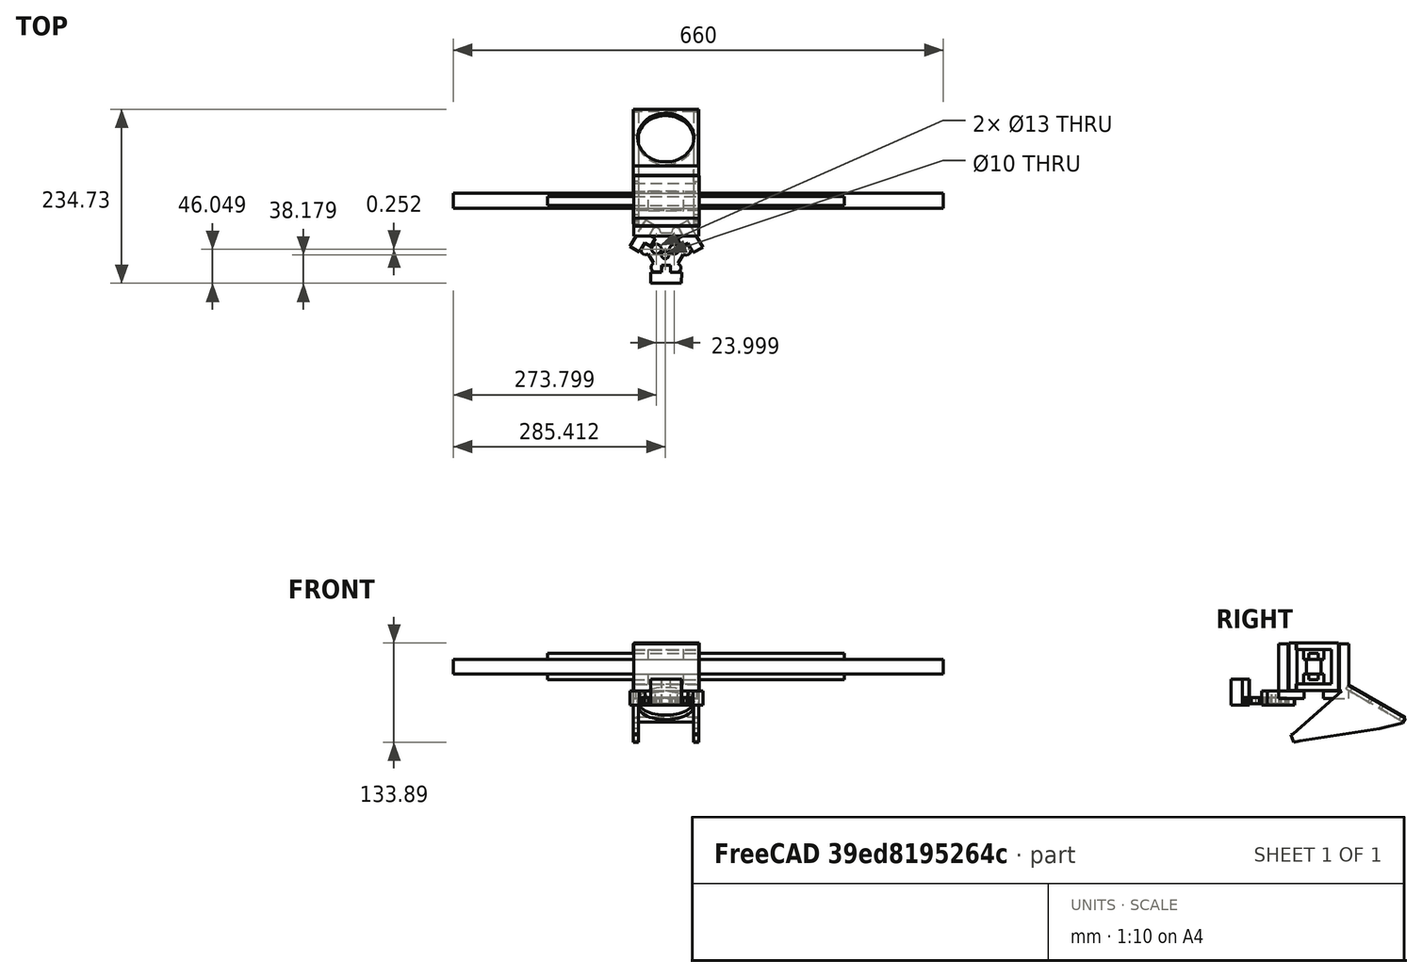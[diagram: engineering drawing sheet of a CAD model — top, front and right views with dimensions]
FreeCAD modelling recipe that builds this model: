
FCSTD DOCUMENT  (FreeCAD 0.17R13522 (Git))
Label: plateX
License: All rights reserved
LicenseURL: http://en.wikipedia.org/wiki/All_rights_reserved
objects: Sketcher::SketchObject×26, Part::Extrusion×26, Part::Box×10, Mesh::Feature×8, Part::MultiFuse×4, App::DocumentObjectGroup×2
note: 66 computed .brp shape members not serialized (recipe doc carries the construction recipe); baked Part::Feature solids carry a one-line shape summary decoded from their .brp

FEATURE [Part::Box] Box  label="vSlot2020"
  AttacherType = Attacher::AttachEngine3D
  Height = 20
  Length = 660
  Placement = pos=(-70,0.5,0) rot=(0,0,1;0rad)
  Width = 20
FEATURE [Part::Box] Box002  label="Rail superior"
  AttacherType = Attacher::AttachEngine3D
  Height = 7.8
  Length = 400
  Placement = pos=(57,4,20) rot=(0,0,1;0rad)
  Width = 12.2
FEATURE [Part::Box] Box004  label="Rail inferior"
  AttacherType = Attacher::AttachEngine3D
  Height = 7.8
  Length = 400
  Placement = pos=(57,4,-7.8) rot=(0,0,1;0rad)
  Width = 12.2
FEATURE [Part::Box] Box005  label="Mgn12h inferior"
  AttacherType = Attacher::AttachEngine3D
  Height = 13
  Length = 47.55
  Placement = pos=(193,-3,-13) rot=(0,0,1;0rad)
  Width = 27.1
FEATURE [Part::Box] Box013  label="Mgn12h superior"
  AttacherType = Attacher::AttachEngine3D
  Height = 13
  Length = 47.55
  Placement = pos=(193,-3,20) rot=(0,0,1;0rad)
  Width = 27.1
FEATURE [Sketcher::SketchObject] Sketch
  sketch-geometry (8):
    g0: LineSegment StartX=64.0547 StartY=96.1652 StartZ=0 EndX=64.0547 EndY=32.1652 EndZ=0
    g1: LineSegment StartX=64.0547 StartY=32.1652 StartZ=0 EndX=121.055 EndY=32.1652 EndZ=0
    g2: LineSegment StartX=121.055 StartY=32.1652 StartZ=0 EndX=121.055 EndY=41.1652 EndZ=0
    g3: LineSegment StartX=121.055 StartY=41.1652 StartZ=0 EndX=74.0547 EndY=41.1652 EndZ=0
    g4: LineSegment StartX=74.0547 StartY=41.1652 StartZ=0 EndX=74.0547 EndY=87.1652 EndZ=0
    g5: LineSegment StartX=74.0547 StartY=87.1652 StartZ=0 EndX=121.055 EndY=87.1652 EndZ=0
    g6: LineSegment StartX=121.055 StartY=87.1652 StartZ=0 EndX=121.055 EndY=96.1652 EndZ=0
    g7: LineSegment StartX=121.055 StartY=96.1652 StartZ=0 EndX=64.0547 EndY=96.1652 EndZ=0
  constraints (22):
    c: Vertical(g0)
    c: Coincident(g0,g1)
    c: Horizontal(g1)
    c: Coincident(g1,g2)
    c: Vertical(g2)
    c: Coincident(g2,g3)
    c: Horizontal(g3)
    c: Coincident(g3,g4)
    c: Vertical(g4)
    c: Coincident(g4,g5)
    c: Horizontal(g5)
    c: Coincident(g5,g6)
    c: Coincident(g6,g7)
    c: Coincident(g7,g0)
    c: Horizontal(g7)
    c: Equal(g7,g1)
    c: Equal(g5,g3)
    c: Equal(g6,g2)
    c: DistanceY(g0,g0) = 64
    c: DistanceX(g7,g7) = 57
    c: DistanceX(g5,g5) = 47
    c: DistanceY(g4,g4) = 46
FEATURE [Part::Extrusion] Extrude  label="PlateX_01"
  Base = -> Sketch
  Dir = (0,0,1)
  DirMode = 2
  FaceMakerClass = Part::FaceMakerBullseye
  LengthFwd = 88
  LengthRev = 0
  Placement = pos=(173,108,74) rot=(0.57735,-0.57735,0.57735;4.18879rad)
  Solid = true
  Symmetric = false
FEATURE [Sketcher::SketchObject] Sketch001
  sketch-geometry (39):
    g0: LineSegment StartX=92.1382 StartY=71.478 StartZ=0 EndX=99.1382 EndY=59.3536 EndZ=0
    g1: LineSegment StartX=68.3387 StartY=30.9498 StartZ=0 EndX=82.3387 EndY=30.9498 EndZ=0
    g2: LineSegment StartX=59.14 StartY=71.8249 StartZ=0 EndX=52.14 EndY=59.7005 EndZ=0
    g3: LineSegment StartX=82.3387 StartY=30.9498 StartZ=0 EndX=83.7847 EndY=26.0283 EndZ=0
    g4: LineSegment StartX=83.7847 StartY=26.0283 StartZ=0 EndX=87.6579 EndY=23.7374 EndZ=0
    g5: LineSegment StartX=87.6579 StartY=23.7374 StartZ=0 EndX=92.6674 EndY=24.8409 EndZ=0
    g6: LineSegment StartX=92.6674 StartY=24.8409 StartZ=0 EndX=98.0127 EndY=33.8785 EndZ=0
    g7: LineSegment StartX=98.0127 StartY=33.8785 StartZ=0 EndX=90.2662 EndY=38.4602 EndZ=0
    g8: LineSegment StartX=90.2662 StartY=38.4602 StartZ=0 EndX=96.3751 EndY=48.7888 EndZ=0
    g9: LineSegment StartX=96.3751 StartY=48.7888 StartZ=0 EndX=104.122 EndY=44.2072 EndZ=0
    g10: LineSegment StartX=104.122 StartY=44.2072 StartZ=0 EndX=109.467 EndY=53.2447 EndZ=0
    g11: LineSegment StartX=109.467 StartY=53.2447 StartZ=0 EndX=108.021 EndY=58.1663 EndZ=0
    g12: LineSegment StartX=108.021 StartY=58.1663 StartZ=0 EndX=104.148 EndY=60.4571 EndZ=0
    g13: LineSegment StartX=104.148 StartY=60.4571 StartZ=0 EndX=99.1382 EndY=59.3536 EndZ=0
    g14: LineSegment StartX=92.1382 StartY=71.478 StartZ=0 EndX=95.6774 EndY=75.191 EndZ=0
    g15: LineSegment StartX=95.6774 StartY=75.191 StartZ=0 EndX=95.7247 EndY=79.6908 EndZ=0
    g16: LineSegment StartX=95.7247 StartY=79.6908 StartZ=0 EndX=92.2644 EndY=83.4773 EndZ=0
    g17: LineSegment StartX=92.2644 StartY=83.4773 StartZ=0 EndX=81.7649 EndY=83.5877 EndZ=0
    g18: LineSegment StartX=81.7649 StartY=83.5877 StartZ=0 EndX=81.6703 EndY=74.5882 EndZ=0
    g19: LineSegment StartX=81.6703 StartY=74.5882 StartZ=0 EndX=69.671 EndY=74.7143 EndZ=0
    g20: LineSegment StartX=69.671 StartY=74.7143 StartZ=0 EndX=69.7656 EndY=83.7138 EndZ=0
    g21: LineSegment StartX=69.7656 StartY=83.7138 StartZ=0 EndX=59.2662 EndY=83.8242 EndZ=0
    g22: LineSegment StartX=59.2662 StartY=83.8242 StartZ=0 EndX=55.727 EndY=80.1112 EndZ=0
    g23: LineSegment StartX=55.727 StartY=80.1112 StartZ=0 EndX=55.6796 EndY=75.6115 EndZ=0
    g24: LineSegment StartX=55.6796 StartY=75.6115 StartZ=0 EndX=59.14 EndY=71.8249 EndZ=0
    g25: LineSegment StartX=52.14 StartY=59.7005 StartZ=0 EndX=47.1537 EndY=60.9041 EndZ=0
    g26: LineSegment StartX=47.1537 StartY=60.9041 StartZ=0 EndX=43.2331 EndY=58.6952 EndZ=0
    g27: LineSegment StartX=43.2331 StartY=58.6952 StartZ=0 EndX=41.6889 EndY=53.8036 EndZ=0
    g28: LineSegment StartX=41.6889 StartY=53.8036 StartZ=0 EndX=46.8412 EndY=44.6589 EndZ=0
    g29: LineSegment StartX=46.8412 StartY=44.6589 StartZ=0 EndX=54.6823 EndY=49.0767 EndZ=0
    g30: LineSegment StartX=54.6823 StartY=49.0767 StartZ=0 EndX=60.5727 EndY=38.6219 EndZ=0
    g31: LineSegment StartX=60.5727 StartY=38.6219 StartZ=0 EndX=52.7316 EndY=34.2041 EndZ=0
    g32: LineSegment StartX=52.7316 StartY=34.2041 StartZ=0 EndX=57.8876 EndY=25.0529 EndZ=0
    g33: LineSegment StartX=57.8876 StartY=25.0529 StartZ=0 EndX=62.874 EndY=23.8493 EndZ=0
    g34: LineSegment StartX=62.874 StartY=23.8493 StartZ=0 EndX=66.7945 EndY=26.0582 EndZ=0
    g35: LineSegment StartX=66.7945 StartY=26.0582 StartZ=0 EndX=68.3387 EndY=30.9498 EndZ=0
    g36: Circle CenterX=76.5882 CenterY=60.6409 CenterZ=0 NormalX=0 NormalY=0 NormalZ=1 AngleXU=0 Radius=5
    g37: Circle CenterX=64.202 CenterY=52.7706 CenterZ=0 NormalX=0 NormalY=0 NormalZ=1 AngleXU=0 Radius=6.5
    g38: Circle CenterX=88.2006 CenterY=52.5183 CenterZ=0 NormalX=0 NormalY=0 NormalZ=1 AngleXU=0 Radius=6.5
  constraints (112):
    c: Angle(g0,g1) = 1.0472
    c: Equal(g2,g0)
    c: Equal(g0,g1)
    c: Distance(g2,g2) = 14
    c: Horizontal(g1)
    c: Angle(g1,g2) = 1.0472
    c: Distance(g0,g1) = 33
    c: Distance(g0,g2) = 33
    c: Distance(g2,g1) = 33
    c: Coincident(g1,g3)
    c: Coincident(g3,g4)
    c: Coincident(g4,g5)
    c: Coincident(g5,g6)
    c: Coincident(g6,g7)
    c: Coincident(g7,g8)
    c: Coincident(g8,g9)
    c: Coincident(g9,g10)
    c: Coincident(g10,g11)
    c: Coincident(g11,g12)
    c: Coincident(g12,g13)
    c: Coincident(g13,g0)
    c: Equal(g10,g6)
    c: Perpendicular(g8,g9)
    c: Perpendicular(g7,g8)
    c: Perpendicular(g10,g9)
    c: Perpendicular(g6,g7)
    c: Equal(g7,g9)
    c: Distance(g7,g6) = 9
    c: Distance(g0,g10) = 12
    c: Distance(g1,g5) = 12
    c: Distance(g11,g9) = 14
    c: Distance(g12,g9) = 14
    c: Distance(g5,g10) = 33
    c: Distance(g4,g7) = 14
    c: Distance(g3,g7) = 14
    c: Equal(g4,g12)
    c: Distance(g3,g4) = 4.5
    c: Equal(g4,g12)
    c: Equal(g5,g3)
    c: Equal(g3,g11)
    c: Equal(g11,g13)
    c: Distance(g8,g7) = 12
    c: Coincident(g0,g14)
    c: Coincident(g14,g15)
    c: Coincident(g15,g16)
    c: Coincident(g16,g17)
    c: Coincident(g17,g18)
    c: Coincident(g18,g19)
    c: Coincident(g19,g20)
    c: Coincident(g20,g21)
    c: Coincident(g21,g22)
    c: Coincident(g22,g23)
    c: Coincident(g23,g24)
    c: Coincident(g24,g2)
    c: Distance(g16,g21) = 33
    c: Distance(g19,g18) = 12
    c: Perpendicular(g20,g19)
    c: Perpendicular(g18,g19)
    c: Perpendicular(g18,g17)
    c: Perpendicular(g21,g20)
    c: Equal(g18,g20)
    c: Equal(g21,g17)
    c: Distance(g18,g17) = 9
    c: Distance(g0,g16) = 12
    c: Distance(g2,g21) = 12
    c: Distance(g22,g20) = 14
    c: Distance(g23,g20) = 14
    c: Distance(g15,g18) = 14
    c: Distance(g14,g18) = 14
    c: Equal(g14,g16)
    c: Equal(g16,g22)
    c: Equal(g22,g24)
    c: Equal(g23,g15)
    c: Distance(g23,g22) = 4.5
    c: Coincident(g2,g25)
    c: Coincident(g25,g26)
    c: Coincident(g26,g27)
    c: Coincident(g27,g28)
    c: Coincident(g28,g29)
    c: Coincident(g29,g30)
    c: Coincident(g30,g31)
    c: Coincident(g31,g32)
    c: Coincident(g32,g33)
    c: Coincident(g33,g34)
    c: Coincident(g34,g35)
    c: Coincident(g35,g1)
    c: Distance(g28,g29) = 9
    c: Equal(g29,g31)
    c: Distance(g29,g30) = 12
    c: Perpendicular(g30,g29)
    c: Perpendicular(g31,g30)
    c: Perpendicular(g29,g28)
    c: Perpendicular(g32,g31)
    c: Distance(g27,g32) = 33
    c: Distance(g2,g27) = 12
    c: Distance(g32,g1) = 12
    c: Distance(g26,g29) = 14
    c: Distance(g25,g29) = 14
    c: Distance(g34,g31) = 14
    c: Distance(g33,g31) = 14
    c: Equal(g26,g34)
    c: Distance(g25,g26) = 4.5
    c: Equal(g25,g27)
    c: Equal(g27,g33)
    c: Equal(g33,g35)
    c: Radius(g37) = 6.5
    c: Radius(g38) = 6.5
    c: Radius(g36) = 5
    c: Distance(g36,g19) = 14
    c: Distance(g37,g38) = 24
    c: Distance(g38,g17) = 31
    c: Distance(g37,g21) = 31
FEATURE [Part::Extrusion] Extrude001  label="SuporteDelta"
  Base = -> Sketch001
  Dir = (0,0,1)
  DirMode = 2
  FaceMakerClass = Part::FaceMakerBullseye
  LengthFwd = 8
  LengthRev = 0
  Placement = pos=(292,-2,-40) rot=(0,0,1;3.14159rad)
  Solid = true
  Symmetric = false
FEATURE [Sketcher::SketchObject] Sketch002
  sketch-geometry (8):
    g0: LineSegment StartX=40.1304 StartY=23.3379 StartZ=0 EndX=40.1304 EndY=69.2379 EndZ=0
    g1: LineSegment StartX=40.1304 StartY=69.2379 StartZ=0 EndX=41.1304 EndY=69.2379 EndZ=0
    g2: LineSegment StartX=41.1304 StartY=69.2379 StartZ=0 EndX=41.1304 EndY=78.2379 EndZ=0
    g3: LineSegment StartX=41.1304 StartY=78.2379 StartZ=0 EndX=51.1304 EndY=78.2379 EndZ=0
    g4: LineSegment StartX=51.1304 StartY=78.2379 StartZ=0 EndX=51.1304 EndY=14.3379 EndZ=0
    g5: LineSegment StartX=51.1304 StartY=14.3379 StartZ=0 EndX=41.1304 EndY=14.3379 EndZ=0
    g6: LineSegment StartX=41.1304 StartY=14.3379 StartZ=0 EndX=41.1304 EndY=23.3379 EndZ=0
    g7: LineSegment StartX=41.1304 StartY=23.3379 StartZ=0 EndX=40.1304 EndY=23.3379 EndZ=0
  constraints (23):
    c: Vertical(g0)
    c: Coincident(g0,g1)
    c: Horizontal(g1)
    c: Coincident(g1,g2)
    c: Coincident(g2,g3)
    c: Horizontal(g3)
    c: Coincident(g3,g4)
    c: Coincident(g4,g5)
    c: Coincident(g5,g6)
    c: Vertical(g6)
    c: Coincident(g6,g7)
    c: Coincident(g7,g0)
    c: Vertical(g2)
    c: Vertical(g4)
    c: Horizontal(g5)
    c: Horizontal(g7)
    c: Equal(g2,g6)
    c: Equal(g3,g5)
    c: Equal(g1,g7)
    c: DistanceY(g0,g0) = 45.9
    c: DistanceY(g2,g2) = 9
    c: DistanceX(g7,g7) = 1
    c: DistanceX(g3,g3) = 10
FEATURE [Part::Extrusion] Extrude002  label="PlateX_02"
  Base = -> Sketch002
  Dir = (0,0,1)
  DirMode = 2
  FaceMakerClass = Part::FaceMakerBullseye
  LengthFwd = 88
  LengthRev = 0
  Placement = pos=(173,28,56) rot=(0.57735,-0.57735,0.57735;4.18879rad)
  Solid = true
  Symmetric = false
FEATURE [Mesh::Feature] hotend_3d_printer  label="hotend-3d-printer"
  Placement = pos=(204,-55,-38) rot=(0,0,1;0rad)
FEATURE [Mesh::Feature] hotend_3d_printer001  label="hotend-3d-printer001"
  Placement = pos=(228,-55,-38) rot=(0,0,1;0rad)
FEATURE [Mesh::Feature] endstop_v1_2_makerbot  label="endstop-X-traseiro-esquerdo"
  Placement = pos=(217,34,-4) rot=(1,0,0;1.5708rad)
FEATURE [Mesh::Feature] endstop_v1_2_makerbot001  label="endstop-X-frontal-direito"
  Placement = pos=(217,-12,-4) rot=(0,0.707107,0.707107;3.14159rad)
FEATURE [Sketcher::SketchObject] Sketch003
  MapMode = 5
  sketch-geometry (8):
    g0: LineSegment StartX=107.535 StartY=111.722 StartZ=0 EndX=107.501 EndY=96.7222 EndZ=0
    g1: LineSegment StartX=107.501 StartY=96.7222 StartZ=0 EndX=92.7007 EndY=96.7558 EndZ=0
    g2: LineSegment StartX=92.7007 StartY=96.7558 StartZ=0 EndX=92.6798 EndY=87.5559 EndZ=0
    g3: LineSegment StartX=92.6798 StartY=87.5559 StartZ=0 EndX=80.7798 EndY=87.5829 EndZ=0
    g4: LineSegment StartX=80.7798 StartY=87.5829 StartZ=0 EndX=80.8007 EndY=96.7829 EndZ=0
    g5: LineSegment StartX=80.8007 StartY=96.7829 StartZ=0 EndX=66.0008 EndY=96.8166 EndZ=0
    g6: LineSegment StartX=66.0008 StartY=96.8166 StartZ=0 EndX=66.0349 EndY=111.817 EndZ=0
    g7: LineSegment StartX=66.0349 StartY=111.817 StartZ=0 EndX=107.535 EndY=111.722 EndZ=0
  constraints (21):
    c: Coincident(g0,g1)
    c: Coincident(g1,g2)
    c: Coincident(g2,g3)
    c: Coincident(g3,g4)
    c: Coincident(g4,g5)
    c: Coincident(g5,g6)
    c: Coincident(g6,g7)
    c: Coincident(g7,g0)
    c: Equal(g2,g4)
    c: Equal(g1,g5)
    c: Perpendicular(g1,g2)
    c: Perpendicular(g2,g3)
    c: Perpendicular(g3,g4)
    c: Perpendicular(g5,g4)
    c: Perpendicular(g6,g5)
    c: Perpendicular(g7,g6)
    c: Perpendicular(g7,g0)
    c: Distance(g2,g3) = 11.9
    c: Distance(g2,g1) = 9.2
    c: Distance(g0,g1) = 14.8
    c: Distance(g0,g0) = 15
FEATURE [Part::Extrusion] Extrude005
  Base = -> Sketch003
  Dir = (0,0,1)
  DirMode = 2
  FaceMakerClass = Part::FaceMakerBullseye
  LengthFwd = 35
  LengthRev = 0
  Solid = true
  Symmetric = false
FEATURE [Sketcher::SketchObject] Sketch004
  MapMode = 5
  sketch-geometry (8):
    g0: LineSegment StartX=114.524 StartY=26.4586 StartZ=0 EndX=101.615 EndY=34.0979 EndZ=0
    g1: LineSegment StartX=101.615 StartY=34.0979 StartZ=0 EndX=109.153 EndY=46.8348 EndZ=0
    g2: LineSegment StartX=109.153 StartY=46.8348 StartZ=0 EndX=101.235 EndY=51.5202 EndZ=0
    g3: LineSegment StartX=101.235 StartY=51.5202 StartZ=0 EndX=107.296 EndY=61.7613 EndZ=0
    g4: LineSegment StartX=107.296 StartY=61.7613 StartZ=0 EndX=115.213 EndY=57.0759 EndZ=0
    g5: LineSegment StartX=115.213 StartY=57.0759 StartZ=0 EndX=122.751 EndY=69.8127 EndZ=0
    g6: LineSegment StartX=122.751 StartY=69.8127 StartZ=0 EndX=135.66 EndY=62.1734 EndZ=0
    g7: LineSegment StartX=135.66 StartY=62.1734 StartZ=0 EndX=114.524 EndY=26.4586 EndZ=0
  constraints (21):
    c: Coincident(g0,g1)
    c: Coincident(g1,g2)
    c: Coincident(g2,g3)
    c: Coincident(g3,g4)
    c: Coincident(g4,g5)
    c: Coincident(g5,g6)
    c: Coincident(g6,g7)
    c: Coincident(g7,g0)
    c: Equal(g2,g4)
    c: Equal(g1,g5)
    c: Perpendicular(g1,g2)
    c: Perpendicular(g2,g3)
    c: Perpendicular(g3,g4)
    c: Perpendicular(g5,g4)
    c: Perpendicular(g6,g5)
    c: Perpendicular(g7,g6)
    c: Perpendicular(g7,g0)
    c: Distance(g2,g3) = 11.9
    c: Distance(g2,g1) = 9.2
    c: Distance(g0,g1) = 14.8
    c: Distance(g0,g0) = 15
FEATURE [Part::Extrusion] Extrude003
  Base = -> Sketch004
  Dir = (0,0,1)
  DirMode = 2
  FaceMakerClass = Part::FaceMakerBullseye
  LengthFwd = 19
  LengthRev = 0
  Solid = true
  Symmetric = false
FEATURE [Sketcher::SketchObject] Sketch005
  MapMode = 5
  sketch-geometry (8):
    g0: LineSegment StartX=37.3535 StartY=63.0419 StartZ=0 EndX=50.4036 EndY=70.4376 EndZ=0
    g1: LineSegment StartX=50.4036 StartY=70.4376 StartZ=0 EndX=57.7007 EndY=57.5616 EndZ=0
    g2: LineSegment StartX=57.7007 StartY=57.5616 StartZ=0 EndX=65.7047 EndY=62.0976 EndZ=0
    g3: LineSegment StartX=65.7047 StartY=62.0976 StartZ=0 EndX=71.572 EndY=51.7446 EndZ=0
    g4: LineSegment StartX=71.572 StartY=51.7446 StartZ=0 EndX=63.5679 EndY=47.2085 EndZ=0
    g5: LineSegment StartX=63.5679 StartY=47.2085 StartZ=0 EndX=70.8651 EndY=34.3325 EndZ=0
    g6: LineSegment StartX=70.8651 StartY=34.3325 StartZ=0 EndX=57.815 EndY=26.9368 EndZ=0
    g7: LineSegment StartX=57.815 StartY=26.9368 StartZ=0 EndX=37.3535 EndY=63.0419 EndZ=0
  constraints (21):
    c: Coincident(g0,g1)
    c: Coincident(g1,g2)
    c: Coincident(g2,g3)
    c: Coincident(g3,g4)
    c: Coincident(g4,g5)
    c: Coincident(g5,g6)
    c: Coincident(g6,g7)
    c: Coincident(g7,g0)
    c: Equal(g2,g4)
    c: Equal(g1,g5)
    c: Perpendicular(g1,g2)
    c: Perpendicular(g2,g3)
    c: Perpendicular(g3,g4)
    c: Perpendicular(g5,g4)
    c: Perpendicular(g6,g5)
    c: Perpendicular(g7,g6)
    c: Perpendicular(g7,g0)
    c: Distance(g2,g3) = 11.9
    c: Distance(g2,g1) = 9.2
    c: Distance(g0,g1) = 14.8
    c: Distance(g0,g0) = 15
FEATURE [Part::Extrusion] Extrude004
  Base = -> Sketch005
  Dir = (0,0,1)
  DirMode = 2
  FaceMakerClass = Part::FaceMakerBullseye
  LengthFwd = 19
  LengthRev = 0
  Solid = true
  Symmetric = false
FEATURE [Sketcher::SketchObject] Sketch006
  MapMode = 5
  sketch-geometry (4):
    g0: LineSegment StartX=39.98 StartY=47.8377 StartZ=0 EndX=39.98 EndY=13.5387 EndZ=0
    g1: LineSegment StartX=39.98 StartY=13.5387 StartZ=0 EndX=127.229 EndY=13.5387 EndZ=0
    g2: LineSegment StartX=127.229 StartY=13.5387 StartZ=0 EndX=127.229 EndY=47.8377 EndZ=0
    g3: LineSegment StartX=127.229 StartY=47.8377 StartZ=0 EndX=39.98 EndY=47.8377 EndZ=0
  constraints (8):
    c: Coincident(g0,g1)
    c: Coincident(g1,g2)
    c: Coincident(g2,g3)
    c: Coincident(g3,g0)
    c: Perpendicular(g2,g1)
    c: Perpendicular(g3,g2)
    c: Perpendicular(g0,g3)
    c: Horizontal(g3)
FEATURE [Sketcher::SketchObject] Sketch007
  MapMode = 5
  sketch-geometry (4):
    g0: LineSegment StartX=39.5777 StartY=47.8687 StartZ=0 EndX=39.5777 EndY=34.8687 EndZ=0
    g1: LineSegment StartX=39.5777 StartY=34.8687 StartZ=0 EndX=127.578 EndY=34.8687 EndZ=0
    g2: LineSegment StartX=127.578 StartY=34.8687 StartZ=0 EndX=127.578 EndY=47.8687 EndZ=0
    g3: LineSegment StartX=127.578 StartY=47.8687 StartZ=0 EndX=39.5777 EndY=47.8687 EndZ=0
  constraints (10):
    c: Coincident(g0,g1)
    c: Coincident(g1,g2)
    c: Coincident(g2,g3)
    c: Coincident(g3,g0)
    c: Perpendicular(g2,g1)
    c: Perpendicular(g3,g2)
    c: Perpendicular(g0,g3)
    c: Horizontal(g3)
    c: DistanceY(g2,g2) = 13
    c: DistanceX(g3,g3) = 88
FEATURE [Part::Extrusion] Extrude006
  Base = -> Sketch007
  Dir = (0,0,1)
  DirMode = 2
  FaceMakerClass = Part::FaceMakerBullseye
  LengthFwd = 64
  LengthRev = 0
  Placement = pos=(3,0,19) rot=(0,0,1;0rad)
  Solid = true
  Symmetric = false
FEATURE [Part::Extrusion] Extrude007
  Base = -> Sketch006
  Dir = (0,0,1)
  DirMode = 2
  FaceMakerClass = Part::FaceMakerBullseye
  LengthFwd = 10
  LengthRev = 0
  Placement = pos=(3,0,9) rot=(0,0,1;0rad)
  Solid = true
  Symmetric = false
FEATURE [Part::MultiFuse] Fusion  label="Suporte1"
  Placement = pos=(303.5,11,-42) rot=(0,0,1;3.14159rad)
  Shapes = -> [Extrude006,Extrude007,Extrude003,Extrude004,Extrude005]
FEATURE [Sketcher::SketchObject] Sketch008
  MapMode = 5
  Placement = pos=(42.5777,14,39) rot=(0.447214,-0.774597,-0.447214;1.82348rad)
  sketch-geometry (8):
    g0: LineSegment StartX=-123.305 StartY=6.07085 StartZ=0 EndX=-123.345 EndY=-1.16956 EndZ=0
    g1: LineSegment StartX=-123.345 StartY=-1.16956 StartZ=0 EndX=-100.407 EndY=-23.6651 EndZ=0
    g2: LineSegment StartX=-9.4672 StartY=-97.368 StartZ=0 EndX=-1.01841 EndY=-90.2813 EndZ=0
    g3: LineSegment StartX=-34.8682 StartY=6.09489 StartZ=0 EndX=-123.305 EndY=6.07085 EndZ=0
    g4: LineSegment StartX=-34.8682 StartY=6.09489 StartZ=0 EndX=-3.03674 EndY=-87.875 EndZ=0
    g5: LineSegment StartX=-3.03674 StartY=-87.875 StartZ=0 EndX=-1.01841 EndY=-90.2813 EndZ=0
    g6: LineSegment StartX=-100.407 StartY=-23.6651 StartZ=0 EndX=-15.5201 EndY=-91.5664 EndZ=0
    g7: LineSegment StartX=-15.5201 StartY=-91.5664 StartZ=0 EndX=-9.4672 EndY=-97.368 EndZ=0
  constraints (9):
    c: Coincident(g0,g1)
    c: Coincident(g3,g0)
    c: Coincident(g3,g4)
    c: Coincident(g4,g5)
    c: Coincident(g5,g2)
    c: Coincident(g1,g6)
    c: Coincident(g6,g7)
    c: Coincident(g7,g2)
    c: Perpendicular(g2,g5)
FEATURE [Part::Extrusion] Extrude011
  Base = -> Sketch008
  Dir = (-1,0,0)
  DirMode = 2
  FaceMakerClass = Part::FaceMakerBullseye
  LengthFwd = 7
  LengthRev = 0
  Placement = pos=(88,0,0) rot=(0,0,1;0rad)
  Solid = true
  Symmetric = false
FEATURE [Sketcher::SketchObject] Sketch009
  MapMode = 5
  sketch-geometry (4):
    g0: LineSegment StartX=39.98 StartY=47.8377 StartZ=0 EndX=39.98 EndY=13.5387 EndZ=0
    g1: LineSegment StartX=39.98 StartY=13.5387 StartZ=0 EndX=127.229 EndY=13.5387 EndZ=0
    g2: LineSegment StartX=127.229 StartY=13.5387 StartZ=0 EndX=127.229 EndY=47.8377 EndZ=0
    g3: LineSegment StartX=127.229 StartY=47.8377 StartZ=0 EndX=39.98 EndY=47.8377 EndZ=0
  constraints (8):
    c: Coincident(g0,g1)
    c: Coincident(g1,g2)
    c: Coincident(g2,g3)
    c: Coincident(g3,g0)
    c: Perpendicular(g2,g1)
    c: Perpendicular(g3,g2)
    c: Perpendicular(g0,g3)
    c: Horizontal(g3)
FEATURE [Part::Extrusion] Extrude010
  Base = -> Sketch009
  Dir = (0,0,1)
  DirMode = 2
  FaceMakerClass = Part::FaceMakerBullseye
  LengthFwd = 10
  LengthRev = 0
  Placement = pos=(3,0,9) rot=(0,0,1;0rad)
  Solid = true
  Symmetric = false
FEATURE [Sketcher::SketchObject] Sketch010
  MapMode = 5
  sketch-geometry (4):
    g0: LineSegment StartX=39.5777 StartY=47.8687 StartZ=0 EndX=39.5777 EndY=34.8687 EndZ=0
    g1: LineSegment StartX=39.5777 StartY=34.8687 StartZ=0 EndX=127.578 EndY=34.8687 EndZ=0
    g2: LineSegment StartX=127.578 StartY=34.8687 StartZ=0 EndX=127.578 EndY=47.8687 EndZ=0
    g3: LineSegment StartX=127.578 StartY=47.8687 StartZ=0 EndX=39.5777 EndY=47.8687 EndZ=0
  constraints (10):
    c: Coincident(g0,g1)
    c: Coincident(g1,g2)
    c: Coincident(g2,g3)
    c: Coincident(g3,g0)
    c: Perpendicular(g2,g1)
    c: Perpendicular(g3,g2)
    c: Perpendicular(g0,g3)
    c: Horizontal(g3)
    c: DistanceY(g2,g2) = 13
    c: DistanceX(g3,g3) = 88
FEATURE [Part::Extrusion] Extrude009
  Base = -> Sketch010
  Dir = (0,0,1)
  DirMode = 2
  FaceMakerClass = Part::FaceMakerBullseye
  LengthFwd = 64
  LengthRev = 0
  Placement = pos=(3,0,19) rot=(0,0,1;0rad)
  Solid = true
  Symmetric = false
FEATURE [Sketcher::SketchObject] Sketch011
  MapMode = 5
  sketch-geometry (5):
    g0: LineSegment StartX=39.1898 StartY=122.876 StartZ=0 EndX=39.1898 EndY=34.8759 EndZ=0
    g1: LineSegment StartX=39.1898 StartY=34.8759 StartZ=0 EndX=127.19 EndY=34.8759 EndZ=0
    g2: LineSegment StartX=127.19 StartY=34.8759 StartZ=0 EndX=127.19 EndY=122.876 EndZ=0
    g3: LineSegment StartX=127.19 StartY=122.876 StartZ=0 EndX=39.1898 EndY=122.876 EndZ=0
    g4: Circle CenterX=83.1898 CenterY=78.8759 CenterZ=0 NormalX=0 NormalY=0 NormalZ=1 AngleXU=0 Radius=38
  constraints (13):
    c: Coincident(g0,g1)
    c: Coincident(g1,g2)
    c: Coincident(g2,g3)
    c: Coincident(g3,g0)
    c: Perpendicular(g2,g1)
    c: Perpendicular(g3,g2)
    c: Perpendicular(g0,g3)
    c: Horizontal(g3)
    c: DistanceY(g2,g2) = 88
    c: DistanceX(g3,g3) = 88
    c: Radius(g4) = 38
    c: DistanceY(g4,g0) = 44
    c: DistanceX(g0,g4) = 44
FEATURE [Part::Extrusion] Extrude012
  Base = -> Sketch011
  Dir = (0,0,1)
  DirMode = 2
  FaceMakerClass = Part::FaceMakerBullseye
  LengthFwd = 7
  LengthRev = 0
  Placement = pos=(3,14,39) rot=(-1,0,0;0.523599rad)
  Solid = true
  Symmetric = false
FEATURE [Sketcher::SketchObject] Sketch012
  MapMode = 5
  Placement = pos=(42.5777,14,39) rot=(0.447214,-0.774597,-0.447214;1.82348rad)
  sketch-geometry (8):
    g0: LineSegment StartX=-123.305 StartY=6.07085 StartZ=0 EndX=-123.345 EndY=-1.16956 EndZ=0
    g1: LineSegment StartX=-123.345 StartY=-1.16956 StartZ=0 EndX=-100.407 EndY=-23.6651 EndZ=0
    g2: LineSegment StartX=-9.4672 StartY=-97.368 StartZ=0 EndX=-1.01841 EndY=-90.2813 EndZ=0
    g3: LineSegment StartX=-34.8682 StartY=6.09489 StartZ=0 EndX=-123.305 EndY=6.07085 EndZ=0
    g4: LineSegment StartX=-34.8682 StartY=6.09489 StartZ=0 EndX=-3.03674 EndY=-87.875 EndZ=0
    g5: LineSegment StartX=-3.03674 StartY=-87.875 StartZ=0 EndX=-1.01841 EndY=-90.2813 EndZ=0
    g6: LineSegment StartX=-100.407 StartY=-23.6651 StartZ=0 EndX=-15.5201 EndY=-91.5664 EndZ=0
    g7: LineSegment StartX=-15.5201 StartY=-91.5664 StartZ=0 EndX=-9.4672 EndY=-97.368 EndZ=0
  constraints (9):
    c: Coincident(g0,g1)
    c: Coincident(g3,g0)
    c: Coincident(g3,g4)
    c: Coincident(g4,g5)
    c: Coincident(g5,g2)
    c: Coincident(g1,g6)
    c: Coincident(g6,g7)
    c: Coincident(g7,g2)
    c: Perpendicular(g2,g5)
FEATURE [Part::Extrusion] Extrude008
  Base = -> Sketch012
  Dir = (-1,0,0)
  DirMode = 2
  FaceMakerClass = Part::FaceMakerBullseye
  LengthFwd = 7
  LengthRev = 0
  Placement = pos=(7,0,0) rot=(0,0,1;0rad)
  Solid = true
  Symmetric = false
FEATURE [Part::MultiFuse] Fusion001  label="Suporte2"
  Placement = pos=(130,10,-42) rot=(0,0,1;0rad)
  Shapes = -> [Extrude009,Extrude008,Extrude010,Extrude011,Extrude012]
FEATURE [App::DocumentObjectGroup] Group  label="Eixo X"
  Group = -> [Box,Box002,Box004,Box005,Box013,Extrude,Extrude001,Extrude002,hotend_3d_printer,hotend_3d_printer001,endstop_v1_2_makerbot,endstop_v1_2_makerbot001,Fusion,Fusion001]
FEATURE [Sketcher::SketchObject] Sketch013
  MapMode = 5
  Placement = pos=(42.5777,14,39) rot=(0.447214,-0.774597,-0.447214;1.82348rad)
  sketch-geometry (8):
    g0: LineSegment StartX=-123.305 StartY=6.07085 StartZ=0 EndX=-123.345 EndY=-1.16956 EndZ=0
    g1: LineSegment StartX=-123.345 StartY=-1.16956 StartZ=0 EndX=-100.407 EndY=-23.6651 EndZ=0
    g2: LineSegment StartX=-9.4672 StartY=-97.368 StartZ=0 EndX=-1.01841 EndY=-90.2813 EndZ=0
    g3: LineSegment StartX=-34.8682 StartY=6.09489 StartZ=0 EndX=-123.305 EndY=6.07085 EndZ=0
    g4: LineSegment StartX=-34.8682 StartY=6.09489 StartZ=0 EndX=-3.03674 EndY=-87.875 EndZ=0
    g5: LineSegment StartX=-3.03674 StartY=-87.875 StartZ=0 EndX=-1.01841 EndY=-90.2813 EndZ=0
    g6: LineSegment StartX=-100.407 StartY=-23.6651 StartZ=0 EndX=-15.5201 EndY=-91.5664 EndZ=0
    g7: LineSegment StartX=-15.5201 StartY=-91.5664 StartZ=0 EndX=-9.4672 EndY=-97.368 EndZ=0
  constraints (9):
    c: Coincident(g0,g1)
    c: Coincident(g3,g0)
    c: Coincident(g3,g4)
    c: Coincident(g4,g5)
    c: Coincident(g5,g2)
    c: Coincident(g1,g6)
    c: Coincident(g6,g7)
    c: Coincident(g7,g2)
    c: Perpendicular(g2,g5)
FEATURE [Sketcher::SketchObject] Sketch014
  MapMode = 5
  sketch-geometry (4):
    g0: LineSegment StartX=39.98 StartY=47.8377 StartZ=0 EndX=39.98 EndY=13.5387 EndZ=0
    g1: LineSegment StartX=39.98 StartY=13.5387 StartZ=0 EndX=127.229 EndY=13.5387 EndZ=0
    g2: LineSegment StartX=127.229 StartY=13.5387 StartZ=0 EndX=127.229 EndY=47.8377 EndZ=0
    g3: LineSegment StartX=127.229 StartY=47.8377 StartZ=0 EndX=39.98 EndY=47.8377 EndZ=0
  constraints (8):
    c: Coincident(g0,g1)
    c: Coincident(g1,g2)
    c: Coincident(g2,g3)
    c: Coincident(g3,g0)
    c: Perpendicular(g2,g1)
    c: Perpendicular(g3,g2)
    c: Perpendicular(g0,g3)
    c: Horizontal(g3)
FEATURE [Sketcher::SketchObject] Sketch015
  MapMode = 5
  sketch-geometry (4):
    g0: LineSegment StartX=39.5777 StartY=47.8687 StartZ=0 EndX=39.5777 EndY=34.8687 EndZ=0
    g1: LineSegment StartX=39.5777 StartY=34.8687 StartZ=0 EndX=127.578 EndY=34.8687 EndZ=0
    g2: LineSegment StartX=127.578 StartY=34.8687 StartZ=0 EndX=127.578 EndY=47.8687 EndZ=0
    g3: LineSegment StartX=127.578 StartY=47.8687 StartZ=0 EndX=39.5777 EndY=47.8687 EndZ=0
  constraints (10):
    c: Coincident(g0,g1)
    c: Coincident(g1,g2)
    c: Coincident(g2,g3)
    c: Coincident(g3,g0)
    c: Perpendicular(g2,g1)
    c: Perpendicular(g3,g2)
    c: Perpendicular(g0,g3)
    c: Horizontal(g3)
    c: DistanceY(g2,g2) = 13
    c: DistanceX(g3,g3) = 88
FEATURE [Sketcher::SketchObject] Sketch016
  MapMode = 5
  sketch-geometry (5):
    g0: LineSegment StartX=39.1898 StartY=122.876 StartZ=0 EndX=39.1898 EndY=34.8759 EndZ=0
    g1: LineSegment StartX=39.1898 StartY=34.8759 StartZ=0 EndX=127.19 EndY=34.8759 EndZ=0
    g2: LineSegment StartX=127.19 StartY=34.8759 StartZ=0 EndX=127.19 EndY=122.876 EndZ=0
    g3: LineSegment StartX=127.19 StartY=122.876 StartZ=0 EndX=39.1898 EndY=122.876 EndZ=0
    g4: Circle CenterX=83.1898 CenterY=78.8759 CenterZ=0 NormalX=0 NormalY=0 NormalZ=1 AngleXU=0 Radius=38
  constraints (13):
    c: Coincident(g0,g1)
    c: Coincident(g1,g2)
    c: Coincident(g2,g3)
    c: Coincident(g3,g0)
    c: Perpendicular(g2,g1)
    c: Perpendicular(g3,g2)
    c: Perpendicular(g0,g3)
    c: Horizontal(g3)
    c: DistanceY(g2,g2) = 88
    c: DistanceX(g3,g3) = 88
    c: Radius(g4) = 38
    c: DistanceY(g4,g0) = 44
    c: DistanceX(g0,g4) = 44
FEATURE [Mesh::Feature] hotend_3d_printer002  label="hotend-3d-printer002"
  Placement = pos=(228,-55,-38) rot=(0,0,1;0rad)
FEATURE [Mesh::Feature] hotend_3d_printer003  label="hotend-3d-printer003"
  Placement = pos=(204,-55,-38) rot=(0,0,1;0rad)
FEATURE [Mesh::Feature] endstop_v1_2_makerbot002  label="endstop-X-traseiro-esquerdo001"
  Placement = pos=(217,34,-4) rot=(1,0,0;1.5708rad)
FEATURE [Mesh::Feature] endstop_v1_2_makerbot003  label="endstop-X-frontal-direito001"
  Placement = pos=(217,-12,-4) rot=(0,0.707107,0.707107;3.14159rad)
FEATURE [Sketcher::SketchObject] Sketch017
  MapMode = 5
  sketch-geometry (4):
    g0: LineSegment StartX=39.98 StartY=47.8377 StartZ=0 EndX=39.98 EndY=13.5387 EndZ=0
    g1: LineSegment StartX=39.98 StartY=13.5387 StartZ=0 EndX=127.229 EndY=13.5387 EndZ=0
    g2: LineSegment StartX=127.229 StartY=13.5387 StartZ=0 EndX=127.229 EndY=47.8377 EndZ=0
    g3: LineSegment StartX=127.229 StartY=47.8377 StartZ=0 EndX=39.98 EndY=47.8377 EndZ=0
  constraints (8):
    c: Coincident(g0,g1)
    c: Coincident(g1,g2)
    c: Coincident(g2,g3)
    c: Coincident(g3,g0)
    c: Perpendicular(g2,g1)
    c: Perpendicular(g3,g2)
    c: Perpendicular(g0,g3)
    c: Horizontal(g3)
FEATURE [Sketcher::SketchObject] Sketch018
  MapMode = 5
  sketch-geometry (4):
    g0: LineSegment StartX=39.5777 StartY=47.8687 StartZ=0 EndX=39.5777 EndY=34.8687 EndZ=0
    g1: LineSegment StartX=39.5777 StartY=34.8687 StartZ=0 EndX=127.578 EndY=34.8687 EndZ=0
    g2: LineSegment StartX=127.578 StartY=34.8687 StartZ=0 EndX=127.578 EndY=47.8687 EndZ=0
    g3: LineSegment StartX=127.578 StartY=47.8687 StartZ=0 EndX=39.5777 EndY=47.8687 EndZ=0
  constraints (10):
    c: Coincident(g0,g1)
    c: Coincident(g1,g2)
    c: Coincident(g2,g3)
    c: Coincident(g3,g0)
    c: Perpendicular(g2,g1)
    c: Perpendicular(g3,g2)
    c: Perpendicular(g0,g3)
    c: Horizontal(g3)
    c: DistanceY(g2,g2) = 13
    c: DistanceX(g3,g3) = 88
FEATURE [Sketcher::SketchObject] Sketch019
  MapMode = 5
  sketch-geometry (8):
    g0: LineSegment StartX=114.524 StartY=26.4586 StartZ=0 EndX=101.615 EndY=34.0979 EndZ=0
    g1: LineSegment StartX=101.615 StartY=34.0979 StartZ=0 EndX=109.153 EndY=46.8348 EndZ=0
    g2: LineSegment StartX=109.153 StartY=46.8348 StartZ=0 EndX=101.235 EndY=51.5202 EndZ=0
    g3: LineSegment StartX=101.235 StartY=51.5202 StartZ=0 EndX=107.296 EndY=61.7613 EndZ=0
    g4: LineSegment StartX=107.296 StartY=61.7613 StartZ=0 EndX=115.213 EndY=57.0759 EndZ=0
    g5: LineSegment StartX=115.213 StartY=57.0759 StartZ=0 EndX=122.751 EndY=69.8127 EndZ=0
    g6: LineSegment StartX=122.751 StartY=69.8127 StartZ=0 EndX=135.66 EndY=62.1734 EndZ=0
    g7: LineSegment StartX=135.66 StartY=62.1734 StartZ=0 EndX=114.524 EndY=26.4586 EndZ=0
  constraints (21):
    c: Coincident(g0,g1)
    c: Coincident(g1,g2)
    c: Coincident(g2,g3)
    c: Coincident(g3,g4)
    c: Coincident(g4,g5)
    c: Coincident(g5,g6)
    c: Coincident(g6,g7)
    c: Coincident(g7,g0)
    c: Equal(g2,g4)
    c: Equal(g1,g5)
    c: Perpendicular(g1,g2)
    c: Perpendicular(g2,g3)
    c: Perpendicular(g3,g4)
    c: Perpendicular(g5,g4)
    c: Perpendicular(g6,g5)
    c: Perpendicular(g7,g6)
    c: Perpendicular(g7,g0)
    c: Distance(g2,g3) = 11.9
    c: Distance(g2,g1) = 9.2
    c: Distance(g0,g1) = 14.8
    c: Distance(g0,g0) = 15
FEATURE [Sketcher::SketchObject] Sketch020
  MapMode = 5
  sketch-geometry (8):
    g0: LineSegment StartX=37.3535 StartY=63.0419 StartZ=0 EndX=50.4036 EndY=70.4376 EndZ=0
    g1: LineSegment StartX=50.4036 StartY=70.4376 StartZ=0 EndX=57.7007 EndY=57.5616 EndZ=0
    g2: LineSegment StartX=57.7007 StartY=57.5616 StartZ=0 EndX=65.7047 EndY=62.0976 EndZ=0
    g3: LineSegment StartX=65.7047 StartY=62.0976 StartZ=0 EndX=71.572 EndY=51.7446 EndZ=0
    g4: LineSegment StartX=71.572 StartY=51.7446 StartZ=0 EndX=63.5679 EndY=47.2085 EndZ=0
    g5: LineSegment StartX=63.5679 StartY=47.2085 StartZ=0 EndX=70.8651 EndY=34.3325 EndZ=0
    g6: LineSegment StartX=70.8651 StartY=34.3325 StartZ=0 EndX=57.815 EndY=26.9368 EndZ=0
    g7: LineSegment StartX=57.815 StartY=26.9368 StartZ=0 EndX=37.3535 EndY=63.0419 EndZ=0
  constraints (21):
    c: Coincident(g0,g1)
    c: Coincident(g1,g2)
    c: Coincident(g2,g3)
    c: Coincident(g3,g4)
    c: Coincident(g4,g5)
    c: Coincident(g5,g6)
    c: Coincident(g6,g7)
    c: Coincident(g7,g0)
    c: Equal(g2,g4)
    c: Equal(g1,g5)
    c: Perpendicular(g1,g2)
    c: Perpendicular(g2,g3)
    c: Perpendicular(g3,g4)
    c: Perpendicular(g5,g4)
    c: Perpendicular(g6,g5)
    c: Perpendicular(g7,g6)
    c: Perpendicular(g7,g0)
    c: Distance(g2,g3) = 11.9
    c: Distance(g2,g1) = 9.2
    c: Distance(g0,g1) = 14.8
    c: Distance(g0,g0) = 15
FEATURE [Sketcher::SketchObject] Sketch021
  MapMode = 5
  sketch-geometry (8):
    g0: LineSegment StartX=107.535 StartY=111.722 StartZ=0 EndX=107.501 EndY=96.7222 EndZ=0
    g1: LineSegment StartX=107.501 StartY=96.7222 StartZ=0 EndX=92.7007 EndY=96.7558 EndZ=0
    g2: LineSegment StartX=92.7007 StartY=96.7558 StartZ=0 EndX=92.6798 EndY=87.5559 EndZ=0
    g3: LineSegment StartX=92.6798 StartY=87.5559 StartZ=0 EndX=80.7798 EndY=87.5829 EndZ=0
    g4: LineSegment StartX=80.7798 StartY=87.5829 StartZ=0 EndX=80.8007 EndY=96.7829 EndZ=0
    g5: LineSegment StartX=80.8007 StartY=96.7829 StartZ=0 EndX=66.0008 EndY=96.8166 EndZ=0
    g6: LineSegment StartX=66.0008 StartY=96.8166 StartZ=0 EndX=66.0349 EndY=111.817 EndZ=0
    g7: LineSegment StartX=66.0349 StartY=111.817 StartZ=0 EndX=107.535 EndY=111.722 EndZ=0
  constraints (21):
    c: Coincident(g0,g1)
    c: Coincident(g1,g2)
    c: Coincident(g2,g3)
    c: Coincident(g3,g4)
    c: Coincident(g4,g5)
    c: Coincident(g5,g6)
    c: Coincident(g6,g7)
    c: Coincident(g7,g0)
    c: Equal(g2,g4)
    c: Equal(g1,g5)
    c: Perpendicular(g1,g2)
    c: Perpendicular(g2,g3)
    c: Perpendicular(g3,g4)
    c: Perpendicular(g5,g4)
    c: Perpendicular(g6,g5)
    c: Perpendicular(g7,g6)
    c: Perpendicular(g7,g0)
    c: Distance(g2,g3) = 11.9
    c: Distance(g2,g1) = 9.2
    c: Distance(g0,g1) = 14.8
    c: Distance(g0,g0) = 15
FEATURE [Part::Extrusion] Extrude014
  Base = -> Sketch013
  Dir = (-1,0,0)
  DirMode = 2
  FaceMakerClass = Part::FaceMakerBullseye
  LengthFwd = 7
  LengthRev = 0
  Placement = pos=(88,0,0) rot=(0,0,1;0rad)
  Solid = true
  Symmetric = false
FEATURE [Part::Extrusion] Extrude015
  Base = -> Sketch016
  Dir = (0,0,1)
  DirMode = 2
  FaceMakerClass = Part::FaceMakerBullseye
  LengthFwd = 7
  LengthRev = 0
  Placement = pos=(3,14,39) rot=(-1,0,0;0.523599rad)
  Solid = true
  Symmetric = false
FEATURE [Sketcher::SketchObject] Sketch022
  sketch-geometry (39):
    g0: LineSegment StartX=92.1382 StartY=71.478 StartZ=0 EndX=99.1382 EndY=59.3536 EndZ=0
    g1: LineSegment StartX=68.3387 StartY=30.9498 StartZ=0 EndX=82.3387 EndY=30.9498 EndZ=0
    g2: LineSegment StartX=59.14 StartY=71.8249 StartZ=0 EndX=52.14 EndY=59.7005 EndZ=0
    g3: LineSegment StartX=82.3387 StartY=30.9498 StartZ=0 EndX=83.7847 EndY=26.0283 EndZ=0
    g4: LineSegment StartX=83.7847 StartY=26.0283 StartZ=0 EndX=87.6579 EndY=23.7374 EndZ=0
    g5: LineSegment StartX=87.6579 StartY=23.7374 StartZ=0 EndX=92.6674 EndY=24.8409 EndZ=0
    g6: LineSegment StartX=92.6674 StartY=24.8409 StartZ=0 EndX=98.0127 EndY=33.8785 EndZ=0
    g7: LineSegment StartX=98.0127 StartY=33.8785 StartZ=0 EndX=90.2662 EndY=38.4602 EndZ=0
    g8: LineSegment StartX=90.2662 StartY=38.4602 StartZ=0 EndX=96.3751 EndY=48.7888 EndZ=0
    g9: LineSegment StartX=96.3751 StartY=48.7888 StartZ=0 EndX=104.122 EndY=44.2072 EndZ=0
    g10: LineSegment StartX=104.122 StartY=44.2072 StartZ=0 EndX=109.467 EndY=53.2447 EndZ=0
    g11: LineSegment StartX=109.467 StartY=53.2447 StartZ=0 EndX=108.021 EndY=58.1663 EndZ=0
    g12: LineSegment StartX=108.021 StartY=58.1663 StartZ=0 EndX=104.148 EndY=60.4571 EndZ=0
    g13: LineSegment StartX=104.148 StartY=60.4571 StartZ=0 EndX=99.1382 EndY=59.3536 EndZ=0
    g14: LineSegment StartX=92.1382 StartY=71.478 StartZ=0 EndX=95.6774 EndY=75.191 EndZ=0
    g15: LineSegment StartX=95.6774 StartY=75.191 StartZ=0 EndX=95.7247 EndY=79.6908 EndZ=0
    g16: LineSegment StartX=95.7247 StartY=79.6908 StartZ=0 EndX=92.2644 EndY=83.4773 EndZ=0
    g17: LineSegment StartX=92.2644 StartY=83.4773 StartZ=0 EndX=81.7649 EndY=83.5877 EndZ=0
    g18: LineSegment StartX=81.7649 StartY=83.5877 StartZ=0 EndX=81.6703 EndY=74.5882 EndZ=0
    g19: LineSegment StartX=81.6703 StartY=74.5882 StartZ=0 EndX=69.671 EndY=74.7143 EndZ=0
    g20: LineSegment StartX=69.671 StartY=74.7143 StartZ=0 EndX=69.7656 EndY=83.7138 EndZ=0
    g21: LineSegment StartX=69.7656 StartY=83.7138 StartZ=0 EndX=59.2662 EndY=83.8242 EndZ=0
    g22: LineSegment StartX=59.2662 StartY=83.8242 StartZ=0 EndX=55.727 EndY=80.1112 EndZ=0
    g23: LineSegment StartX=55.727 StartY=80.1112 StartZ=0 EndX=55.6796 EndY=75.6115 EndZ=0
    g24: LineSegment StartX=55.6796 StartY=75.6115 StartZ=0 EndX=59.14 EndY=71.8249 EndZ=0
    g25: LineSegment StartX=52.14 StartY=59.7005 StartZ=0 EndX=47.1537 EndY=60.9041 EndZ=0
    g26: LineSegment StartX=47.1537 StartY=60.9041 StartZ=0 EndX=43.2331 EndY=58.6952 EndZ=0
    g27: LineSegment StartX=43.2331 StartY=58.6952 StartZ=0 EndX=41.6889 EndY=53.8036 EndZ=0
    g28: LineSegment StartX=41.6889 StartY=53.8036 StartZ=0 EndX=46.8412 EndY=44.6589 EndZ=0
    g29: LineSegment StartX=46.8412 StartY=44.6589 StartZ=0 EndX=54.6823 EndY=49.0767 EndZ=0
    g30: LineSegment StartX=54.6823 StartY=49.0767 StartZ=0 EndX=60.5727 EndY=38.6219 EndZ=0
    g31: LineSegment StartX=60.5727 StartY=38.6219 StartZ=0 EndX=52.7316 EndY=34.2041 EndZ=0
    g32: LineSegment StartX=52.7316 StartY=34.2041 StartZ=0 EndX=57.8876 EndY=25.0529 EndZ=0
    g33: LineSegment StartX=57.8876 StartY=25.0529 StartZ=0 EndX=62.874 EndY=23.8493 EndZ=0
    g34: LineSegment StartX=62.874 StartY=23.8493 StartZ=0 EndX=66.7945 EndY=26.0582 EndZ=0
    g35: LineSegment StartX=66.7945 StartY=26.0582 StartZ=0 EndX=68.3387 EndY=30.9498 EndZ=0
    g36: Circle CenterX=76.5882 CenterY=60.6409 CenterZ=0 NormalX=0 NormalY=0 NormalZ=1 AngleXU=0 Radius=5
    g37: Circle CenterX=64.202 CenterY=52.7706 CenterZ=0 NormalX=0 NormalY=0 NormalZ=1 AngleXU=0 Radius=6.5
    g38: Circle CenterX=88.2006 CenterY=52.5183 CenterZ=0 NormalX=0 NormalY=0 NormalZ=1 AngleXU=0 Radius=6.5
  constraints (112):
    c: Angle(g0,g1) = 1.0472
    c: Equal(g2,g0)
    c: Equal(g0,g1)
    c: Distance(g2,g2) = 14
    c: Horizontal(g1)
    c: Angle(g1,g2) = 1.0472
    c: Distance(g0,g1) = 33
    c: Distance(g0,g2) = 33
    c: Distance(g2,g1) = 33
    c: Coincident(g1,g3)
    c: Coincident(g3,g4)
    c: Coincident(g4,g5)
    c: Coincident(g5,g6)
    c: Coincident(g6,g7)
    c: Coincident(g7,g8)
    c: Coincident(g8,g9)
    c: Coincident(g9,g10)
    c: Coincident(g10,g11)
    c: Coincident(g11,g12)
    c: Coincident(g12,g13)
    c: Coincident(g13,g0)
    c: Equal(g10,g6)
    c: Perpendicular(g8,g9)
    c: Perpendicular(g7,g8)
    c: Perpendicular(g10,g9)
    c: Perpendicular(g6,g7)
    c: Equal(g7,g9)
    c: Distance(g7,g6) = 9
    c: Distance(g0,g10) = 12
    c: Distance(g1,g5) = 12
    c: Distance(g11,g9) = 14
    c: Distance(g12,g9) = 14
    c: Distance(g5,g10) = 33
    c: Distance(g4,g7) = 14
    c: Distance(g3,g7) = 14
    c: Equal(g4,g12)
    c: Distance(g3,g4) = 4.5
    c: Equal(g4,g12)
    c: Equal(g5,g3)
    c: Equal(g3,g11)
    c: Equal(g11,g13)
    c: Distance(g8,g7) = 12
    c: Coincident(g0,g14)
    c: Coincident(g14,g15)
    c: Coincident(g15,g16)
    c: Coincident(g16,g17)
    c: Coincident(g17,g18)
    c: Coincident(g18,g19)
    c: Coincident(g19,g20)
    c: Coincident(g20,g21)
    c: Coincident(g21,g22)
    c: Coincident(g22,g23)
    c: Coincident(g23,g24)
    c: Coincident(g24,g2)
    c: Distance(g16,g21) = 33
    c: Distance(g19,g18) = 12
    c: Perpendicular(g20,g19)
    c: Perpendicular(g18,g19)
    c: Perpendicular(g18,g17)
    c: Perpendicular(g21,g20)
    c: Equal(g18,g20)
    c: Equal(g21,g17)
    c: Distance(g18,g17) = 9
    c: Distance(g0,g16) = 12
    c: Distance(g2,g21) = 12
    c: Distance(g22,g20) = 14
    c: Distance(g23,g20) = 14
    c: Distance(g15,g18) = 14
    c: Distance(g14,g18) = 14
    c: Equal(g14,g16)
    c: Equal(g16,g22)
    c: Equal(g22,g24)
    c: Equal(g23,g15)
    c: Distance(g23,g22) = 4.5
    c: Coincident(g2,g25)
    c: Coincident(g25,g26)
    c: Coincident(g26,g27)
    c: Coincident(g27,g28)
    c: Coincident(g28,g29)
    c: Coincident(g29,g30)
    c: Coincident(g30,g31)
    c: Coincident(g31,g32)
    c: Coincident(g32,g33)
    c: Coincident(g33,g34)
    c: Coincident(g34,g35)
    c: Coincident(g35,g1)
    c: Distance(g28,g29) = 9
    c: Equal(g29,g31)
    c: Distance(g29,g30) = 12
    c: Perpendicular(g30,g29)
    c: Perpendicular(g31,g30)
    c: Perpendicular(g29,g28)
    c: Perpendicular(g32,g31)
    c: Distance(g27,g32) = 33
    c: Distance(g2,g27) = 12
    c: Distance(g32,g1) = 12
    c: Distance(g26,g29) = 14
    c: Distance(g25,g29) = 14
    c: Distance(g34,g31) = 14
    c: Distance(g33,g31) = 14
    c: Equal(g26,g34)
    c: Distance(g25,g26) = 4.5
    c: Equal(g25,g27)
    c: Equal(g27,g33)
    c: Equal(g33,g35)
    c: Radius(g37) = 6.5
    c: Radius(g38) = 6.5
    c: Radius(g36) = 5
    c: Distance(g36,g19) = 14
    c: Distance(g37,g38) = 24
    c: Distance(g38,g17) = 31
    c: Distance(g37,g21) = 31
FEATURE [Sketcher::SketchObject] Sketch023
  sketch-geometry (8):
    g0: LineSegment StartX=64.0547 StartY=96.1652 StartZ=0 EndX=64.0547 EndY=32.1652 EndZ=0
    g1: LineSegment StartX=64.0547 StartY=32.1652 StartZ=0 EndX=121.055 EndY=32.1652 EndZ=0
    g2: LineSegment StartX=121.055 StartY=32.1652 StartZ=0 EndX=121.055 EndY=41.1652 EndZ=0
    g3: LineSegment StartX=121.055 StartY=41.1652 StartZ=0 EndX=74.0547 EndY=41.1652 EndZ=0
    g4: LineSegment StartX=74.0547 StartY=41.1652 StartZ=0 EndX=74.0547 EndY=87.1652 EndZ=0
    g5: LineSegment StartX=74.0547 StartY=87.1652 StartZ=0 EndX=121.055 EndY=87.1652 EndZ=0
    g6: LineSegment StartX=121.055 StartY=87.1652 StartZ=0 EndX=121.055 EndY=96.1652 EndZ=0
    g7: LineSegment StartX=121.055 StartY=96.1652 StartZ=0 EndX=64.0547 EndY=96.1652 EndZ=0
  constraints (22):
    c: Vertical(g0)
    c: Coincident(g0,g1)
    c: Horizontal(g1)
    c: Coincident(g1,g2)
    c: Vertical(g2)
    c: Coincident(g2,g3)
    c: Horizontal(g3)
    c: Coincident(g3,g4)
    c: Vertical(g4)
    c: Coincident(g4,g5)
    c: Horizontal(g5)
    c: Coincident(g5,g6)
    c: Coincident(g6,g7)
    c: Coincident(g7,g0)
    c: Horizontal(g7)
    c: Equal(g7,g1)
    c: Equal(g5,g3)
    c: Equal(g6,g2)
    c: DistanceY(g0,g0) = 64
    c: DistanceX(g7,g7) = 57
    c: DistanceX(g5,g5) = 47
    c: DistanceY(g4,g4) = 46
FEATURE [Part::Extrusion] Extrude013  label="PlateX_003"
  Base = -> Sketch023
  Dir = (0,0,1)
  DirMode = 2
  FaceMakerClass = Part::FaceMakerBullseye
  LengthFwd = 88
  LengthRev = 0
  Placement = pos=(173,108,74) rot=(0.57735,-0.57735,0.57735;4.18879rad)
  Solid = true
  Symmetric = false
FEATURE [Sketcher::SketchObject] Sketch024
  sketch-geometry (8):
    g0: LineSegment StartX=40.1304 StartY=23.3379 StartZ=0 EndX=40.1304 EndY=69.2379 EndZ=0
    g1: LineSegment StartX=40.1304 StartY=69.2379 StartZ=0 EndX=41.1304 EndY=69.2379 EndZ=0
    g2: LineSegment StartX=41.1304 StartY=69.2379 StartZ=0 EndX=41.1304 EndY=78.2379 EndZ=0
    g3: LineSegment StartX=41.1304 StartY=78.2379 StartZ=0 EndX=51.1304 EndY=78.2379 EndZ=0
    g4: LineSegment StartX=51.1304 StartY=78.2379 StartZ=0 EndX=51.1304 EndY=14.3379 EndZ=0
    g5: LineSegment StartX=51.1304 StartY=14.3379 StartZ=0 EndX=41.1304 EndY=14.3379 EndZ=0
    g6: LineSegment StartX=41.1304 StartY=14.3379 StartZ=0 EndX=41.1304 EndY=23.3379 EndZ=0
    g7: LineSegment StartX=41.1304 StartY=23.3379 StartZ=0 EndX=40.1304 EndY=23.3379 EndZ=0
  constraints (23):
    c: Vertical(g0)
    c: Coincident(g0,g1)
    c: Horizontal(g1)
    c: Coincident(g1,g2)
    c: Coincident(g2,g3)
    c: Horizontal(g3)
    c: Coincident(g3,g4)
    c: Coincident(g4,g5)
    c: Coincident(g5,g6)
    c: Vertical(g6)
    c: Coincident(g6,g7)
    c: Coincident(g7,g0)
    c: Vertical(g2)
    c: Vertical(g4)
    c: Horizontal(g5)
    c: Horizontal(g7)
    c: Equal(g2,g6)
    c: Equal(g3,g5)
    c: Equal(g1,g7)
    c: DistanceY(g0,g0) = 45.9
    c: DistanceY(g2,g2) = 9
    c: DistanceX(g7,g7) = 1
    c: DistanceX(g3,g3) = 10
FEATURE [Part::Extrusion] Extrude016
  Base = -> Sketch020
  Dir = (0,0,1)
  DirMode = 2
  FaceMakerClass = Part::FaceMakerBullseye
  LengthFwd = 19
  LengthRev = 0
  Solid = true
  Symmetric = false
FEATURE [Part::Extrusion] Extrude017
  Base = -> Sketch015
  Dir = (0,0,1)
  DirMode = 2
  FaceMakerClass = Part::FaceMakerBullseye
  LengthFwd = 64
  LengthRev = 0
  Placement = pos=(3,0,19) rot=(0,0,1;0rad)
  Solid = true
  Symmetric = false
FEATURE [Part::Extrusion] Extrude018
  Base = -> Sketch014
  Dir = (0,0,1)
  DirMode = 2
  FaceMakerClass = Part::FaceMakerBullseye
  LengthFwd = 10
  LengthRev = 0
  Placement = pos=(3,0,9) rot=(0,0,1;0rad)
  Solid = true
  Symmetric = false
FEATURE [Part::Extrusion] Extrude019
  Base = -> Sketch021
  Dir = (0,0,1)
  DirMode = 2
  FaceMakerClass = Part::FaceMakerBullseye
  LengthFwd = 35
  LengthRev = 0
  Solid = true
  Symmetric = false
FEATURE [Part::Extrusion] Extrude020
  Base = -> Sketch018
  Dir = (0,0,1)
  DirMode = 2
  FaceMakerClass = Part::FaceMakerBullseye
  LengthFwd = 64
  LengthRev = 0
  Placement = pos=(3,0,19) rot=(0,0,1;0rad)
  Solid = true
  Symmetric = false
FEATURE [Part::Extrusion] Extrude021
  Base = -> Sketch017
  Dir = (0,0,1)
  DirMode = 2
  FaceMakerClass = Part::FaceMakerBullseye
  LengthFwd = 10
  LengthRev = 0
  Placement = pos=(3,0,9) rot=(0,0,1;0rad)
  Solid = true
  Symmetric = false
FEATURE [Part::Extrusion] Extrude022
  Base = -> Sketch019
  Dir = (0,0,1)
  DirMode = 2
  FaceMakerClass = Part::FaceMakerBullseye
  LengthFwd = 19
  LengthRev = 0
  Solid = true
  Symmetric = false
FEATURE [Part::MultiFuse] Fusion003  label="Suporte004"
  Placement = pos=(303.5,11,-42) rot=(0,0,1;3.14159rad)
  Shapes = -> [Extrude020,Extrude021,Extrude022,Extrude016,Extrude019]
FEATURE [Part::Extrusion] Extrude024  label="PlateX_004"
  Base = -> Sketch024
  Dir = (0,0,1)
  DirMode = 2
  FaceMakerClass = Part::FaceMakerBullseye
  LengthFwd = 88
  LengthRev = 0
  Placement = pos=(173,28,56) rot=(0.57735,-0.57735,0.57735;4.18879rad)
  Solid = true
  Symmetric = false
FEATURE [Part::Box] Box014  label="Mgn12h inferior001"
  AttacherType = Attacher::AttachEngine3D
  Height = 13
  Length = 47.55
  Placement = pos=(193,-3,-13) rot=(0,0,1;0rad)
  Width = 27.1
FEATURE [Part::Box] Box015  label="Rail superior001"
  AttacherType = Attacher::AttachEngine3D
  Height = 7.8
  Length = 400
  Placement = pos=(57,4,20) rot=(0,0,1;0rad)
  Width = 12.2
FEATURE [Part::Box] Box016  label="Mgn12h superior001"
  AttacherType = Attacher::AttachEngine3D
  Height = 13
  Length = 47.55
  Placement = pos=(193,-3,20) rot=(0,0,1;0rad)
  Width = 27.1
FEATURE [Part::Box] Box017  label="Rail inferior001"
  AttacherType = Attacher::AttachEngine3D
  Height = 7.8
  Length = 400
  Placement = pos=(57,4,-7.8) rot=(0,0,1;0rad)
  Width = 12.2
FEATURE [Part::Box] Box018  label="vSlot2021"
  AttacherType = Attacher::AttachEngine3D
  Height = 20
  Length = 660
  Placement = pos=(-70,0.5,0) rot=(0,0,1;0rad)
  Width = 20
FEATURE [Part::Extrusion] Extrude025  label="SuporteDelta001"
  Base = -> Sketch022
  Dir = (0,0,1)
  DirMode = 2
  FaceMakerClass = Part::FaceMakerBullseye
  LengthFwd = 8
  LengthRev = 0
  Placement = pos=(292,-2,-40) rot=(0,0,1;3.14159rad)
  Solid = true
  Symmetric = false
FEATURE [Sketcher::SketchObject] Sketch025
  MapMode = 5
  Placement = pos=(42.5777,14,39) rot=(0.447214,-0.774597,-0.447214;1.82348rad)
  sketch-geometry (8):
    g0: LineSegment StartX=-123.305 StartY=6.07085 StartZ=0 EndX=-123.345 EndY=-1.16956 EndZ=0
    g1: LineSegment StartX=-123.345 StartY=-1.16956 StartZ=0 EndX=-100.407 EndY=-23.6651 EndZ=0
    g2: LineSegment StartX=-9.4672 StartY=-97.368 StartZ=0 EndX=-1.01841 EndY=-90.2813 EndZ=0
    g3: LineSegment StartX=-34.8682 StartY=6.09489 StartZ=0 EndX=-123.305 EndY=6.07085 EndZ=0
    g4: LineSegment StartX=-34.8682 StartY=6.09489 StartZ=0 EndX=-3.03674 EndY=-87.875 EndZ=0
    g5: LineSegment StartX=-3.03674 StartY=-87.875 StartZ=0 EndX=-1.01841 EndY=-90.2813 EndZ=0
    g6: LineSegment StartX=-100.407 StartY=-23.6651 StartZ=0 EndX=-15.5201 EndY=-91.5664 EndZ=0
    g7: LineSegment StartX=-15.5201 StartY=-91.5664 StartZ=0 EndX=-9.4672 EndY=-97.368 EndZ=0
  constraints (9):
    c: Coincident(g0,g1)
    c: Coincident(g3,g0)
    c: Coincident(g3,g4)
    c: Coincident(g4,g5)
    c: Coincident(g5,g2)
    c: Coincident(g1,g6)
    c: Coincident(g6,g7)
    c: Coincident(g7,g2)
    c: Perpendicular(g2,g5)
FEATURE [Part::Extrusion] Extrude023
  Base = -> Sketch025
  Dir = (-1,0,0)
  DirMode = 2
  FaceMakerClass = Part::FaceMakerBullseye
  LengthFwd = 7
  LengthRev = 0
  Placement = pos=(7,0,0) rot=(0,0,1;0rad)
  Solid = true
  Symmetric = false
FEATURE [Part::MultiFuse] Fusion002  label="Suporte003"
  Placement = pos=(130,10,-42) rot=(0,0,1;0rad)
  Shapes = -> [Extrude017,Extrude023,Extrude018,Extrude014,Extrude015]
FEATURE [App::DocumentObjectGroup] Group001  label="Eixo X001"
  Group = -> [Box018,Box015,Box017,Box014,Box016,Extrude013,Extrude025,Extrude024,hotend_3d_printer003,hotend_3d_printer002,endstop_v1_2_makerbot002,endstop_v1_2_makerbot003,Fusion003,Fusion002]
